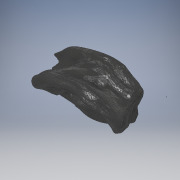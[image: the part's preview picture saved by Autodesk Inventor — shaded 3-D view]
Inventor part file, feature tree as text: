
AUTODESK INVENTOR PART (.ipt)
format: ipt  version: 2019 (Build 230136000, 136)  size: 18,084,864 bytes
history: native  units: in
note: dims shown in document units (in); Inventor stores cm internally (conversion verified against a paired STEP export)
features: other x5, plane x2, surface_op x1, direct_edit x1
ambient origin geometry x8: Origin, YZ Plane, XZ Plane, XY Plane, X Axis, Y Axis, Z Axis, Center Point
bodies: Solid1 (feature_tree)
feature tree (9):
  other  "ear_right_cut"
  surface_op  "Stitch Surface1"
  direct_edit  "Direct Edit1"
  other  "Work Axis1"
  plane  "Work Plane1"
  plane  "Work Plane2"
  other  "Composite1"
  other  "Srf1"
  other  "Scale1"
